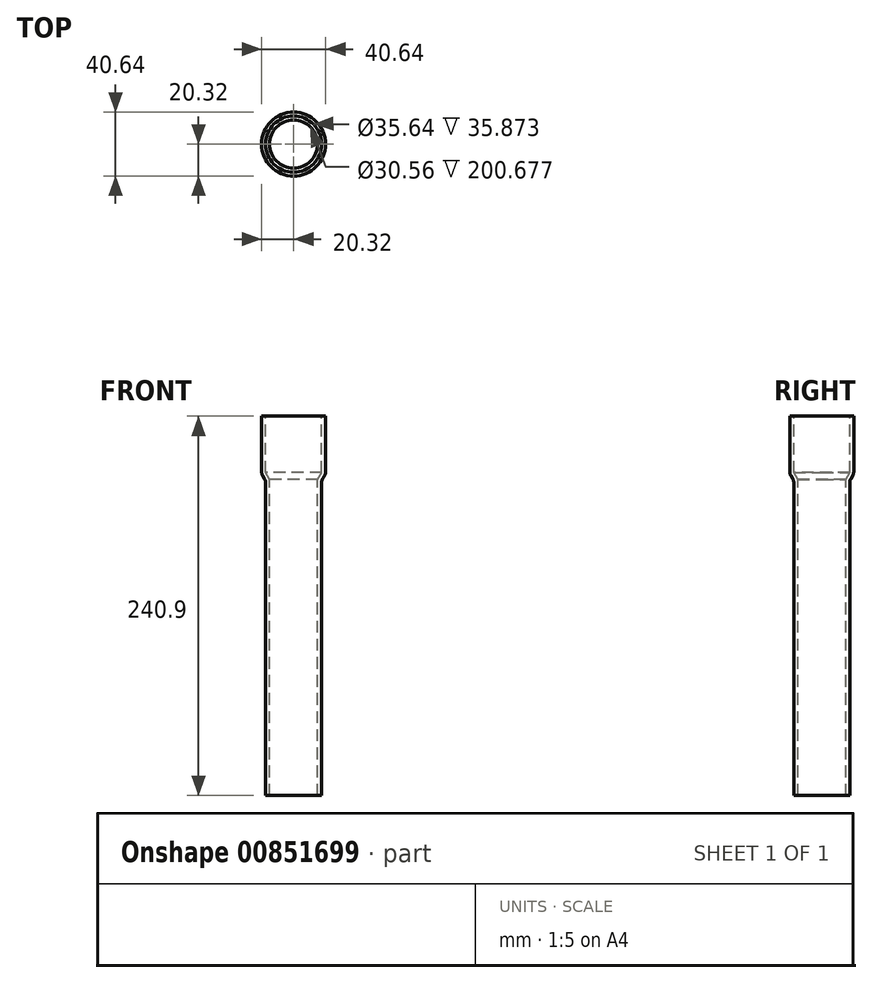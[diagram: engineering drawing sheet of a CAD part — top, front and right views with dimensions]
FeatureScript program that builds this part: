
annotation { "Feature Type Name" : "Feature", "Feature Type Description" : "" }
export const myFeature = defineFeature(function(context is Context, id is Id, definition is map)
    precondition{}
    {
        {
            var Q0;
            Q0=qCreatedBy(makeId("Front.planeOp"),FACE);
            var sketch = newSketch(context, id + "F0", { "sketchPlane" : qUnion([Q0])});
            skLineSegment(sketch, "E0", {"start": v(20.32, 51.76) * mm, "end": v(20.32, 15.2) * mm});
            skLineSegment(sketch, "E1", {"start": v(20.32, 15.2) * mm, "end": v(17.78, 10.86) * mm});
            skLineSegment(sketch, "E2", {"start": v(17.78, 10.86) * mm, "end": v(17.78, -189.14) * mm});
            skLineSegment(sketch, "E3", {"start": v(17.78, -189.14) * mm, "end": v(0, -189.14) * mm});
            skLineSegment(sketch, "E4", {"start": v(20.32, 51.76) * mm, "end": v(0, 51.76) * mm});
            skLineSegment(sketch, "E5", {"start": v(0, 51.76) * mm, "end": v(0, -189.14) * mm});
            skSolve(sketch);
        }
        {
            var Q0;
            Q0=makeQuery(id+"F0.imprint","IMPRINT",FACE,{"disambiguationData":[TD([[makeQuery(id+"F0.imprint","IMPRINT",EDGE,{"derivedFrom":sQuery(id+"F0.wireOp",EDGE,"E0")}),-1.0]])]});
            var Q1;
            Q1=sQuery(id+"F0.wireOp",EDGE,"E5");
            revolve(context, id + "F1", {"surfaceOperationType" : NewSurfaceOperationType.NEW, "entities" : qUnion([Q0]), "axis" : qUnion([Q1]), "revolveType" : RevolveType.FULL});
        }
        {
            var Q0;
            Q0=makeQuery(id+"F1.opRevolve","SWEPT_FACE",FACE,{"disambiguationData":[OSD([sQuery(id+"F0.wireOp",EDGE,"E4")])]});
            var Q1;
            Q1=makeQuery(id+"F1.opRevolve","SWEPT_FACE",FACE,{"disambiguationData":[OSD([sQuery(id+"F0.wireOp",EDGE,"E3")])]});
            shell(context, id + "F2", {"entities" : qUnion([Q0, Q1]), "thickness" : 2.5 * mm});
        }
        {
            var Q0;
            Q0=makeQuery(id+"F1.opRevolve","SWEPT_FACE",FACE,{"disambiguationData":[OSD([sQuery(id+"F0.wireOp",EDGE,"E1")])]});
            fillet(context, id + "F3", {"entities" : qUnion([Q0]), "radius" : 5 * mm, "tangentPropagation" : true, "allowEdgeOverflow" : false});
        }
    });
